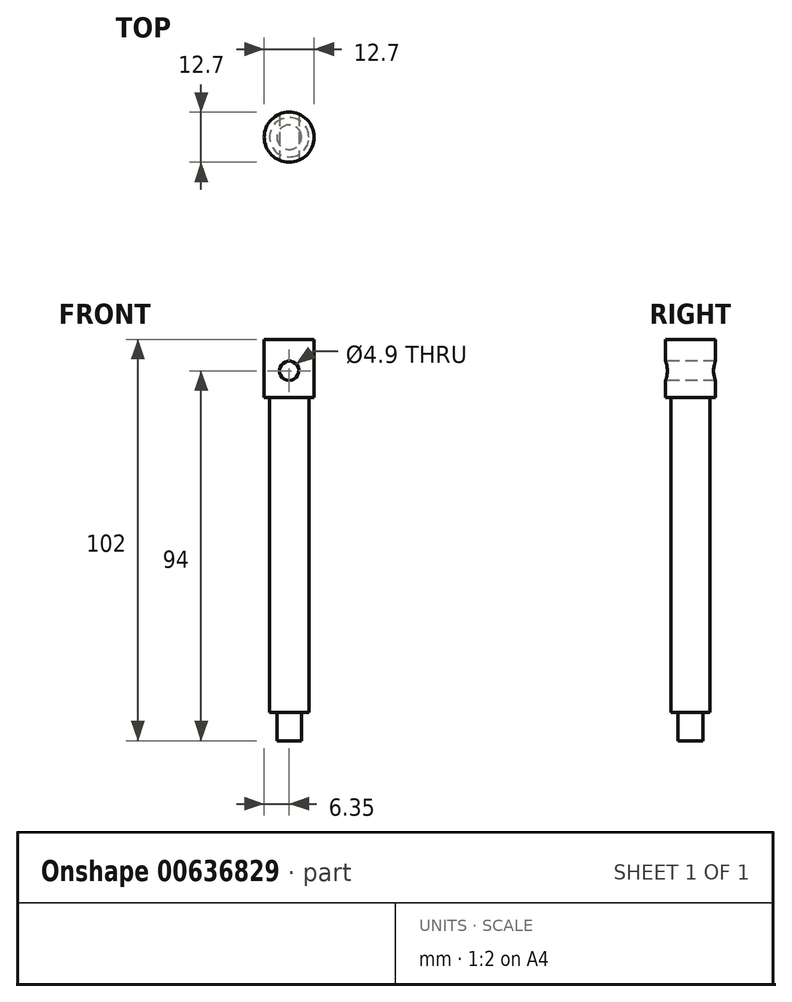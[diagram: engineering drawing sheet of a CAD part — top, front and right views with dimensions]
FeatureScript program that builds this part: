
annotation { "Feature Type Name" : "Feature", "Feature Type Description" : "" }
export const myFeature = defineFeature(function(context is Context, id is Id, definition is map)
    precondition{}
    {
        {
            var Q0;
            Q0=qCreatedBy(makeId("Right.planeOp"),FACE);
            var sketch = newSketch(context, id + "F0", { "sketchPlane" : qUnion([Q0])});
            skLineSegment(sketch, "E0", {"start": v(0, 51) * mm, "end": v(-6.35, 51) * mm});
            skLineSegment(sketch, "E1", {"start": v(-6.35, 51) * mm, "end": v(-6.35, 36.2) * mm});
            skLineSegment(sketch, "E2", {"start": v(-6.35, 36.2) * mm, "end": v(-5, 36.2) * mm});
            skLineSegment(sketch, "E3", {"start": v(-5, 36.2) * mm, "end": v(-5, -43.8) * mm});
            skLineSegment(sketch, "E4", {"start": v(-5, -43.8) * mm, "end": v(-3.12, -43.8) * mm});
            skLineSegment(sketch, "E5", {"start": v(-3.12, -43.8) * mm, "end": v(-3.12, -51) * mm});
            skLineSegment(sketch, "E6", {"start": v(-3.12, -51) * mm, "end": v(0, -51) * mm});
            skLineSegment(sketch, "E7", {"start": v(0, -51) * mm, "end": v(0, 51) * mm});
            skLineSegment(sketch, "E8", {"start": v(0, 69.59) * mm, "end": v(0, -62.48) * mm, "construction": true});
            skPoint(sketch, "E9", {"position": v(0, 0) * mm});
            skSolve(sketch);
        }
        {
            var Q0;
            Q0=makeQuery(id+"F0.imprint","IMPRINT",FACE,{"disambiguationData":[TD([[makeQuery(id+"F0.imprint","IMPRINT",EDGE,{"derivedFrom":sQuery(id+"F0.wireOp",EDGE,"E0")}),1.0]])]});
            var Q1;
            Q1=sQuery(id+"F0.wireOp",EDGE,"E7");
            revolve(context, id + "F1", {"entities" : qUnion([Q0]), "axis" : qUnion([Q1]), "revolveType" : RevolveType.FULL});
        }
        {
            var Q0;
            Q0=qCreatedBy(makeId("Front.planeOp"),FACE);
            cPlane(context, id + "F2", {"entities" : qUnion([Q0]), "cplaneType" : CPlaneType.OFFSET, "offset" : 13.3 * mm, "width" : 150 * mm, "height" : 150 * mm});
        }
        {
            var Q0;
            Q0=qCreatedBy(id+"F2.planeOp",FACE);
            var sketch = newSketch(context, id + "F3", { "sketchPlane" : qUnion([Q0])});
            skCircle(sketch, "E10", {"center": v(0, 43) * mm, "radius": 2.45 * mm});
            skSolve(sketch);
        }
        {
            var Q0;
            Q0=makeQuery(id+"F3.imprint","IMPRINT",FACE,{"disambiguationData":[TD([[makeQuery(id+"F3.imprint","IMPRINT",EDGE,{"derivedFrom":sQuery(id+"F3.wireOp",EDGE,"E10")}),1.0]])]});
            extrude(context, id + "F4", {"entities" : qUnion([Q0]), "operationType" : NewBodyOperationType.REMOVE, "endBound" : BoundingType.THROUGH_ALL, "oppositeDirection" : true, "depth" : 25 * mm, "offsetDistance" : 25 * mm});
        }
    });
